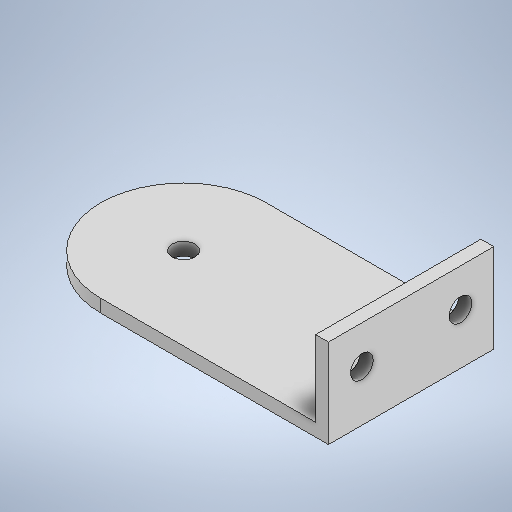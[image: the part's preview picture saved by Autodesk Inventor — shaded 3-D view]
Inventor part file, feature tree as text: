
AUTODESK INVENTOR PART (.ipt)
format: ipt  version: 2025.2 (Build 292293000, 293)  size: 262,144 bytes
history: native  units: in
note: dims shown in document units (in); Inventor stores cm internally (conversion verified against a paired STEP export)
features: extrude x4, sketch x4
ambient origin geometry x8: Origin, YZ Plane, XZ Plane, XY Plane, X Axis, Y Axis, Z Axis, Center Point
bodies: Solid1 (feature_tree)
feature tree (8):
  extrude  "Extrusion1"  Depth=0.4291in
  extrude  "Extrusion2"  Depth=0.8583in
  extrude  "Extrusion3"  Depth=0.0669in
  extrude  "Extrusion4"  Depth=0.0669in
  sketch  "Sketch1"  dims[d2=0.4291in d3=1.1811in]
  sketch  "Sketch2"  dims[d4=1.1811in d5=0.8583in]
  sketch  "Sketch3"  dims[d6=0.0669in d7=0.0in d8=0.1181in]
  sketch  "Sketch4"  dims[d9=0.0669in d10=0.0in d11=0.0669in d12=0.3937in d13=0.0in d14=0.1181in d15=0.1181in d16=0.5118in d17=0.0in d18=0.1969in d19=0.1732in d20=0.3937in d21=0.0in]
